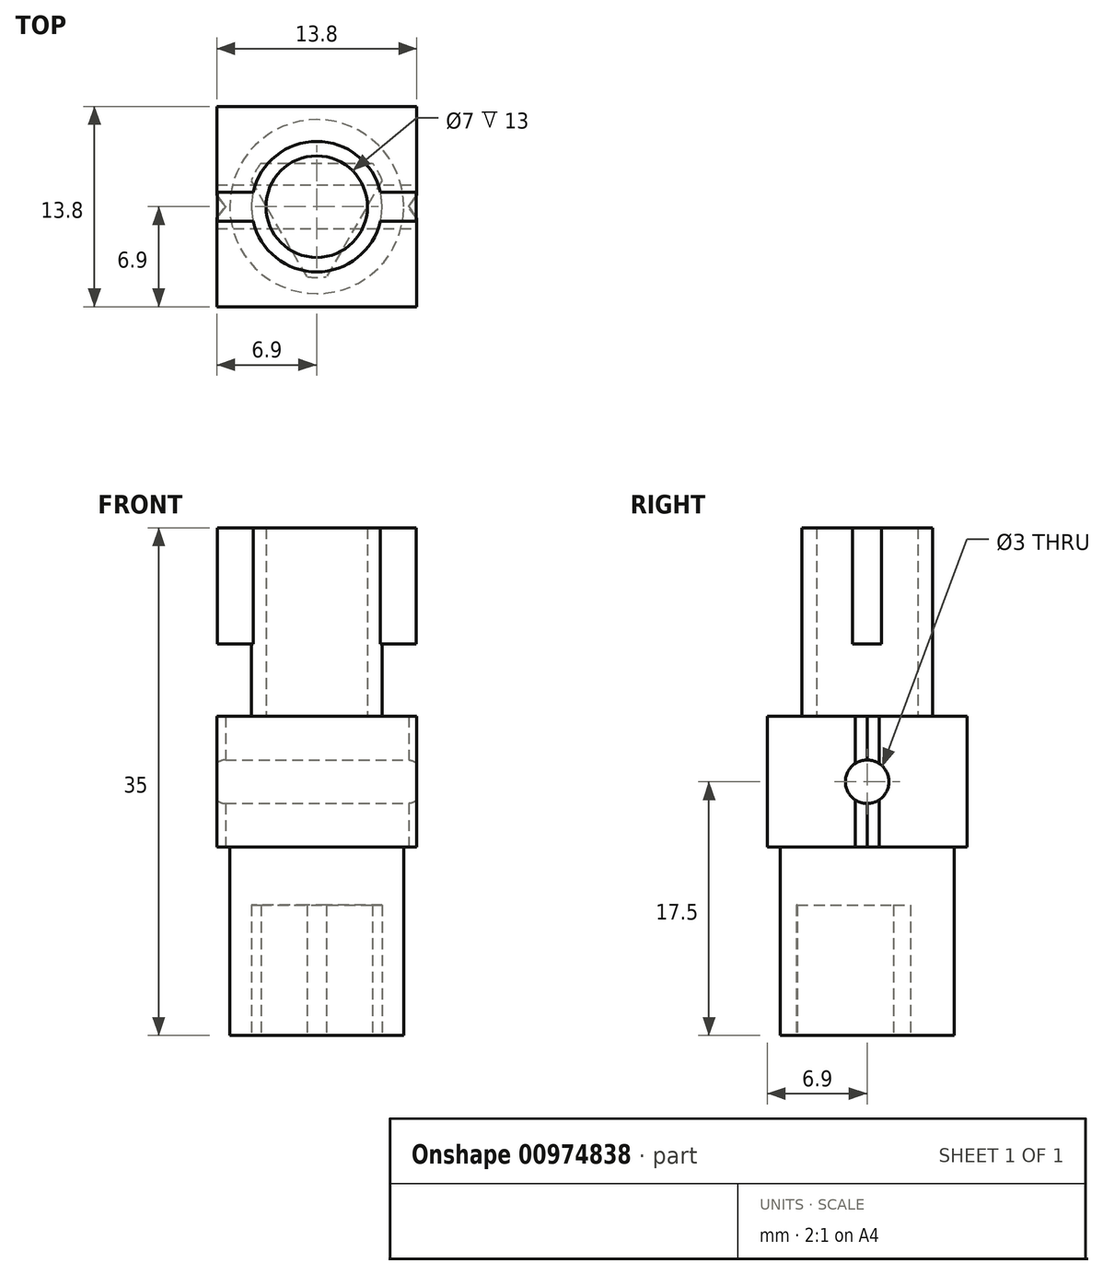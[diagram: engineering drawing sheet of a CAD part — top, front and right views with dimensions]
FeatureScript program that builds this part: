
annotation { "Feature Type Name" : "Feature", "Feature Type Description" : "" }
export const myFeature = defineFeature(function(context is Context, id is Id, definition is map)
    precondition{}
    {
        {
            var Q0;
            Q0=qCreatedBy(makeId("Top.planeOp"),FACE);
            var sketch = newSketch(context, id + "F0", { "sketchPlane" : qUnion([Q0])});
            skLineSegment(sketch, "E0.bottom", {"start": v(6.9, 6.9) * mm, "end": v(-6.9, 6.9) * mm});
            skLineSegment(sketch, "E0.top", {"start": v(6.9, -6.9) * mm, "end": v(-6.9, -6.9) * mm});
            skLineSegment(sketch, "E0.left", {"start": v(6.9, 6.9) * mm, "end": v(6.9, -6.9) * mm});
            skLineSegment(sketch, "E0.right", {"start": v(-6.9, 6.9) * mm, "end": v(-6.9, -6.9) * mm});
            skSolve(sketch);
        }
        {
            var Q0;
            Q0=qSketchRegion(id+"F0",true);
            extrude(context, id + "F1", {"entities" : qUnion([Q0]), "endBound" : BoundingType.SYMMETRIC, "depth" : 9 * mm, "offsetDistance" : 25 * mm});
        }
        {
            var Q0;
            Q0=makeQuery(id+"F1.opExtrude","CAP_FACE",FACE,{"disambiguationData":[OSD([sQuery(id+"F0.wireOp",EDGE,"E0.bottom"),sQuery(id+"F0.wireOp",EDGE,"E0.top"),sQuery(id+"F0.wireOp",EDGE,"E0.left"),sQuery(id+"F0.wireOp",EDGE,"E0.right")])],"isStart":false});
            var sketch = newSketch(context, id + "F2", { "sketchPlane" : qUnion([Q0])});
            skCircle(sketch, "E1", {"center": v(0, 0) * mm, "radius": 4.5 * mm});
            skCircle(sketch, "E2", {"center": v(0, 0) * mm, "radius": 3.5 * mm});
            skSolve(sketch);
        }
        {
            var Q0;
            Q0=qSketchRegion(id+"F2",true);
            extrude(context, id + "F3", {"entities" : qUnion([Q0]), "depth" : 13 * mm, "offsetDistance" : 25 * mm});
        }
        {
            var Q0;
            Q0=makeQuery(id+"F1.opExtrude","CAP_FACE",FACE,{"disambiguationData":[OSD([sQuery(id+"F0.wireOp",EDGE,"E0.bottom"),sQuery(id+"F0.wireOp",EDGE,"E0.top"),sQuery(id+"F0.wireOp",EDGE,"E0.left"),sQuery(id+"F0.wireOp",EDGE,"E0.right")])],"isStart":true});
            var sketch = newSketch(context, id + "F4", { "sketchPlane" : qUnion([Q0])});
            skCircle(sketch, "E3", {"center": v(0, 0) * mm, "radius": 6 * mm});
            skSolve(sketch);
        }
        {
            var Q0;
            Q0=qSketchRegion(id+"F4",true);
            extrude(context, id + "F5", {"entities" : qUnion([Q0]), "depth" : 13 * mm, "offsetDistance" : 25 * mm});
        }
        {
            var Q0;
            Q0=makeQuery(id+"F1.opExtrude","SWEPT_FACE",FACE,{"disambiguationData":[OSD([sQuery(id+"F0.wireOp",EDGE,"E0.left")])]});
            var sketch = newSketch(context, id + "F6", { "sketchPlane" : qUnion([Q0])});
            skCircle(sketch, "E4", {"center": v(0, 0) * mm, "radius": 1.5 * mm});
            skSolve(sketch);
        }
        {
            var Q0;
            Q0=qSketchRegion(id+"F6",true);
            extrude(context, id + "F7", {"entities" : qUnion([Q0]), "operationType" : NewBodyOperationType.REMOVE, "endBound" : BoundingType.THROUGH_ALL, "oppositeDirection" : true, "depth" : 25 * mm, "offsetDistance" : 25 * mm});
        }
        {
            var Q0;
            Q0=makeQuery(id+"F1.opExtrude","CAP_FACE",FACE,{"disambiguationData":[OSD([sQuery(id+"F0.wireOp",EDGE,"E0.bottom"),sQuery(id+"F0.wireOp",EDGE,"E0.top"),sQuery(id+"F0.wireOp",EDGE,"E0.left"),sQuery(id+"F0.wireOp",EDGE,"E0.right")])],"isStart":true});
            var sketch = newSketch(context, id + "F8", { "sketchPlane" : qUnion([Q0])});
            skLineSegment(sketch, "E5", {"start": v(6.34, 0) * mm, "end": v(6.9, 0.83) * mm});
            skLineSegment(sketch, "E6", {"start": v(6.34, 0) * mm, "end": v(6.9, -0.83) * mm});
            skLineSegment(sketch, "E7", {"start": v(6.9, 0.83) * mm, "end": v(6.9, -0.83) * mm});
            skLineSegment(sketch, "E8", {"start": v(-6.3, 0) * mm, "end": v(-6.9, 0.8) * mm});
            skLineSegment(sketch, "E9", {"start": v(-6.3, 0) * mm, "end": v(-6.9, -0.8) * mm});
            skLineSegment(sketch, "E10", {"start": v(-6.9, -0.8) * mm, "end": v(-6.9, 0.8) * mm});
            skSolve(sketch);
        }
        {
            var Q0;
            Q0=qSketchRegion(id+"F8",true);
            extrude(context, id + "F9", {"entities" : qUnion([Q0]), "operationType" : NewBodyOperationType.REMOVE, "endBound" : BoundingType.THROUGH_ALL, "oppositeDirection" : true, "depth" : 25 * mm, "offsetDistance" : 25 * mm});
        }
        {
            var Q0;
            Q0=makeQuery(id+"F3.opExtrude","CAP_FACE",FACE,{"disambiguationData":[OSD([sQuery(id+"F2.wireOp",EDGE,"E1"),sQuery(id+"F2.wireOp",EDGE,"E2")])],"isStart":false});
            var sketch = newSketch(context, id + "F10", { "sketchPlane" : qUnion([Q0])});
            skLineSegment(sketch, "E11", {"start": v(-6.85, -1) * mm, "end": v(-3.62, -1) * mm});
            skLineSegment(sketch, "E12", {"start": v(6.85, 1) * mm, "end": v(3.62, 1) * mm});
            skLineSegment(sketch, "E13", {"start": v(-6.85, 1) * mm, "end": v(-6.85, -1) * mm});
            skLineSegment(sketch, "E14", {"start": v(6.85, 1) * mm, "end": v(6.85, -1) * mm});
            skLineSegment(sketch, "E15.trimOffspring", {"start": v(-3.62, 1) * mm, "end": v(-6.85, 1) * mm});
            skLineSegment(sketch, "E16.trimOffspring", {"start": v(3.62, -1) * mm, "end": v(6.85, -1) * mm});
            skPoint(sketch, "E17.center.orphan", {"position": v(0, 0) * mm});
            skLineSegment(sketch, "E18", {"start": v(-3.62, 1) * mm, "end": v(-3.62, -1) * mm});
            skLineSegment(sketch, "E19", {"start": v(3.62, 1) * mm, "end": v(3.62, -1) * mm});
            skSolve(sketch);
        }
        {
            var Q0;
            Q0=qSketchRegion(id+"F10",true);
            extrude(context, id + "F11", {"entities" : qUnion([Q0]), "operationType" : NewBodyOperationType.ADD, "oppositeDirection" : true, "depth" : 8 * mm, "offsetDistance" : 25 * mm});
        }
        {
            var Q0;
            Q0=makeQuery(id+"F5.opExtrude","CAP_FACE",FACE,{"disambiguationData":[OSD([sQuery(id+"F4.wireOp",EDGE,"E3")])],"isStart":false});
            var sketch = newSketch(context, id + "F12", { "sketchPlane" : qUnion([Q0])});
            skArc(sketch, "E20", {"start": v(0.68, 4.83) * mm, "mid": v(0, 4.88) * mm, "end": v(-0.68, 4.83) * mm});
            skLineSegment(sketch, "E21", {"start": v(-0.68, 4.83) * mm, "end": v(-4.52, -1.83) * mm});
            skLineSegment(sketch, "E22", {"start": v(-3.84, -3) * mm, "end": v(3.84, -3) * mm});
            skLineSegment(sketch, "E23", {"start": v(4.52, -1.83) * mm, "end": v(0.68, 4.83) * mm});
            skPoint(sketch, "E24.orphan", {"position": v(0, 6) * mm});
            skArc(sketch, "E25.trimOffspring", {"start": v(-4.52, -1.83) * mm, "mid": v(-4.22, -2.44) * mm, "end": v(-3.84, -3) * mm});
            skArc(sketch, "E26.trimOffspring", {"start": v(3.84, -3) * mm, "mid": v(4.22, -2.44) * mm, "end": v(4.52, -1.83) * mm});
            skSolve(sketch);
        }
        {
            var Q0;
            Q0=makeQuery(id+"F12.imprint","IMPRINT",FACE,{"disambiguationData":[TD([[makeQuery(id+"F12.imprint","IMPRINT",EDGE,{"derivedFrom":sQuery(id+"F12.wireOp",EDGE,"E20")}),1.0]])]});
            extrude(context, id + "F13", {"entities" : qUnion([Q0]), "operationType" : NewBodyOperationType.REMOVE, "oppositeDirection" : true, "depth" : 9 * mm, "offsetDistance" : 25 * mm});
        }
    });
